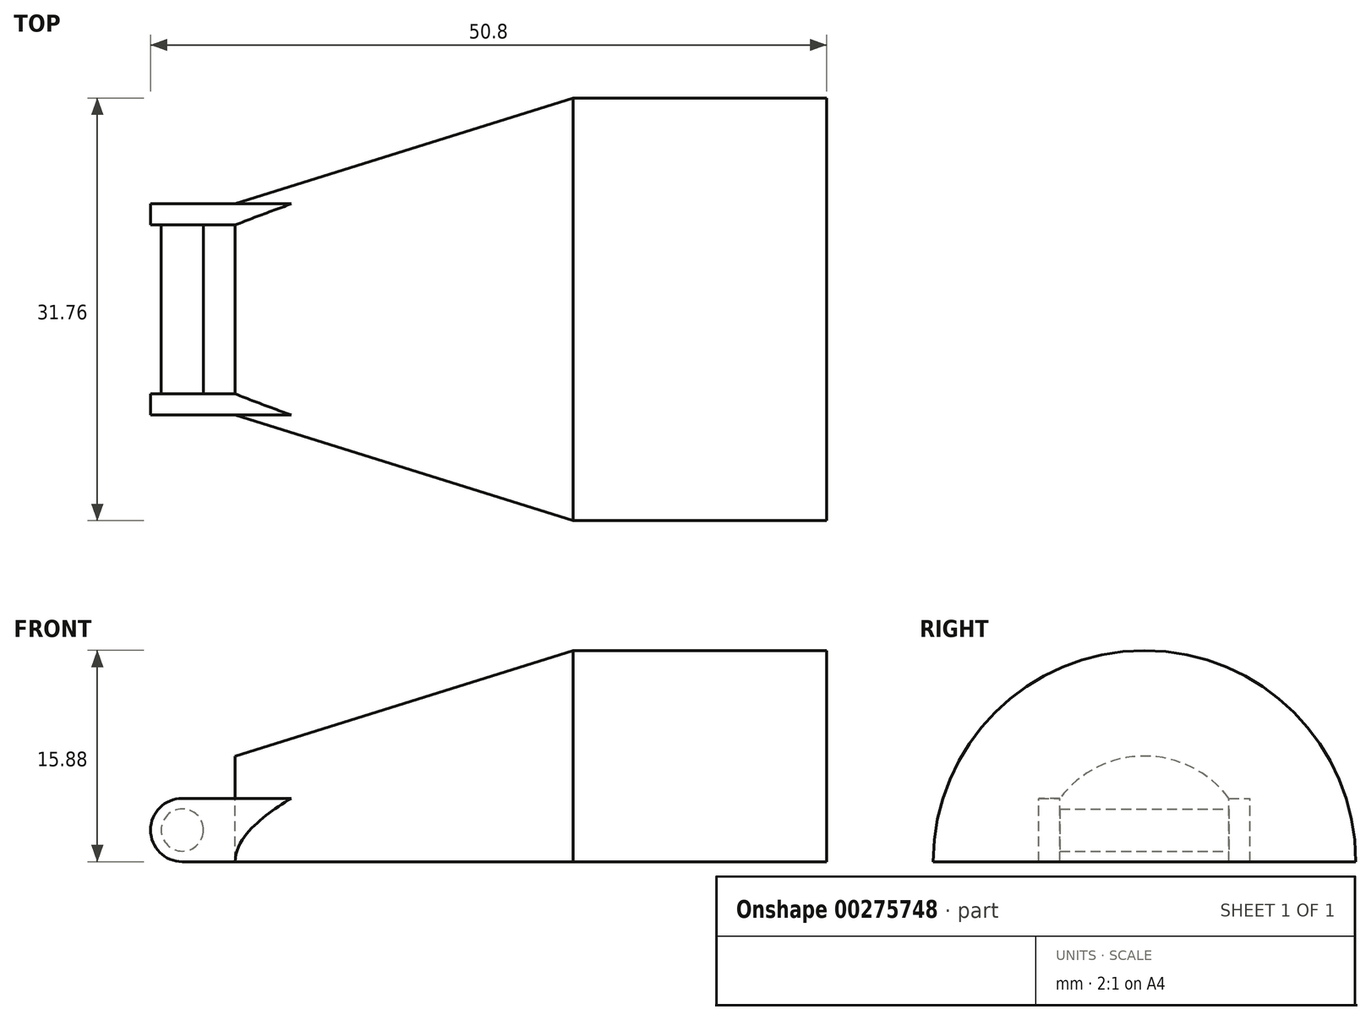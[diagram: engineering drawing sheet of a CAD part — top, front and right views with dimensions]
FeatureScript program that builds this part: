
annotation { "Feature Type Name" : "Feature", "Feature Type Description" : "" }
export const myFeature = defineFeature(function(context is Context, id is Id, definition is map)
    precondition{}
    {
        {
            var Q0;
            Q0=qCreatedBy(makeId("Right.planeOp"),FACE);
            var sketch = newSketch(context, id + "F0", { "sketchPlane" : qUnion([Q0])});
            skLineSegment(sketch, "E0", {"start": v(-15.88, 0) * mm, "end": v(15.88, 0) * mm});
            skCircle(sketch, "E1", {"center": v(0, 0) * mm, "radius": 15.88 * mm});
            skSolve(sketch);
        }
        {
            var Q0;
            Q0=qCreatedBy(makeId("Right.planeOp"),FACE);
            cPlane(context, id + "F1", {"entities" : qUnion([Q0]), "cplaneType" : CPlaneType.OFFSET, "offset" : 25.4 * mm, "oppositeDirection" : true, "width" : 152.4 * mm, "height" : 152.4 * mm});
        }
        {
            var Q0;
            Q0=qCreatedBy(id+"F1.planeOp",FACE);
            var sketch = newSketch(context, id + "F2", { "sketchPlane" : qUnion([Q0])});
            skCircle(sketch, "E2", {"center": v(0, 0) * mm, "radius": 7.94 * mm});
            skLineSegment(sketch, "E3", {"start": v(-7.94, 0) * mm, "end": v(7.94, 0) * mm});
            skSolve(sketch);
        }
        {
            var Q0;
            {var subQ0=sQuery(id+"F2.wireOp",EDGE,"E3");Q0=makeQuery(id+"F2.imprint","IMPRINT",FACE,{"disambiguationData":[TD([[makeQuery(id+"F2.imprint","IMPRINT",EDGE,{"derivedFrom":subQ0}),1.0]])]});}
            var Q1;
            {var subQ0=sQuery(id+"F0.wireOp",EDGE,"E0");Q1=makeQuery(id+"F0.imprint","IMPRINT",FACE,{"disambiguationData":[TD([[makeQuery(id+"F0.imprint","IMPRINT",EDGE,{"derivedFrom":subQ0}),1.0]])]});}
            loft(context, id + "F3", {"sheetProfilesArray" : [{ "sheetProfileEntities" : qUnion([Q0]) }, { "sheetProfileEntities" : qUnion([Q1]) }]});
        }
        {
            var Q0;
            {var subQ0=sQuery(id+"F0.wireOp",EDGE,"E0");Q0=makeQuery(id+"F3.opLoft","CAP_FACE",FACE,{"disambiguationData":[OSD([makeQuery(id+"F0.imprint","IMPRINT",FACE,{"disambiguationData":[TD([[makeQuery(id+"F0.imprint","IMPRINT",EDGE,{"derivedFrom":subQ0}),1.0]])]})])],"isStart":true});}
            extrude(context, id + "F4", {"entities" : qUnion([Q0]), "operationType" : NewBodyOperationType.ADD, "depth" : 19.05 * mm});
        }
        {
            var Q0;
            {var subQ0=sQuery(id+"F2.wireOp",EDGE,"E3");Q0=makeQuery(id+"F3.opLoft","CAP_FACE",FACE,{"disambiguationData":[OSD([makeQuery(id+"F2.imprint","IMPRINT",FACE,{"disambiguationData":[TD([[makeQuery(id+"F2.imprint","IMPRINT",EDGE,{"derivedFrom":subQ0}),1.0]])]})])],"isStart":true});}
            var sketch = newSketch(context, id + "F5", { "sketchPlane" : qUnion([Q0])});
            skLineSegment(sketch, "E4.bottom", {"start": v(-7.94, 0) * mm, "end": v(-6.35, 0) * mm});
            skLineSegment(sketch, "E4.top", {"start": v(-7.94, 4.76) * mm, "end": v(-6.35, 4.76) * mm});
            skLineSegment(sketch, "E4.left", {"start": v(-7.94, 0) * mm, "end": v(-7.94, 4.76) * mm});
            skLineSegment(sketch, "E4.right", {"start": v(-6.35, 0) * mm, "end": v(-6.35, 4.76) * mm});
            skPoint(sketch, "E5.endSnap0", {"position": v(0, 0) * mm});
            skLineSegment(sketch, "E6.MirrorCS", {"start": v(7.94, 0) * mm, "end": v(6.35, 0) * mm});
            skLineSegment(sketch, "E7.MirrorCS", {"start": v(7.94, 0) * mm, "end": v(7.94, 4.76) * mm});
            skLineSegment(sketch, "E8.MirrorCS", {"start": v(6.35, 0) * mm, "end": v(6.35, 4.76) * mm});
            skLineSegment(sketch, "E9.MirrorCS", {"start": v(7.94, 4.76) * mm, "end": v(6.35, 4.76) * mm});
            skSolve(sketch);
        }
        {
            var Q0;
            Q0=qSketchRegion(id+"F5",true);
            extrude(context, id + "F6", {"entities" : qUnion([Q0]), "operationType" : NewBodyOperationType.ADD, "endBound" : BoundingType.SYMMETRIC, "depth" : 12.7 * mm});
        }
        {
            var Q0;
            Q0=makeQuery(id+"F6.opExtrude","SWEPT_FACE",FACE,{"disambiguationData":[OSD([sQuery(id+"F5.wireOp",EDGE,"E4.left")])]});
            var sketch = newSketch(context, id + "F7", { "sketchPlane" : qUnion([Q0])});
            skPoint(sketch, "E10", {"position": v(31.75, 2.38) * mm});
            skLineSegment(sketch, "E11", {"start": v(31.75, 2.38) * mm, "end": v(29.37, 2.38) * mm});
            skCircle(sketch, "E12", {"center": v(29.37, 2.38) * mm, "radius": 2.38 * mm});
            skCircle(sketch, "E13", {"center": v(29.37, 2.38) * mm, "radius": 1.59 * mm});
            skSolve(sketch);
        }
        {
            var Q0;
            {var subQ0=sQuery(id+"F7.wireOp",EDGE,"E12");var subQ1=sQuery(id+"F5.wireOp",EDGE,"E4.left");var subQ2=makeQuery(id+"F6.opExtrude","CAP_EDGE",EDGE,{"disambiguationData":[OSD([subQ1])],"isStart":false});var subQ3=makeQuery(id+"F7.imprint","INTERSECT",VERTEX,{"derivedFrom":[subQ2,subQ0]});Q0=makeQuery(id+"F7.imprint","IMPRINT",FACE,{"disambiguationData":[TD([[makeQuery(id+"F7.imprint","IMPRINT",EDGE,{"disambiguationData":[TD([[subQ3,-1.0]])],"derivedFrom":subQ0}),-1.0]])]});}
            var Q1;
            {var subQ0=sQuery(id+"F7.wireOp",EDGE,"E12");var subQ1=sQuery(id+"F5.wireOp",EDGE,"E4.left");var subQ2=makeQuery(id+"F6.opExtrude","CAP_EDGE",EDGE,{"disambiguationData":[OSD([subQ1])],"isStart":false});var subQ3=makeQuery(id+"F7.imprint","INTERSECT",VERTEX,{"derivedFrom":[subQ2,subQ0]});Q1=makeQuery(id+"F7.imprint","IMPRINT",FACE,{"disambiguationData":[TD([[makeQuery(id+"F7.imprint","IMPRINT",EDGE,{"disambiguationData":[TD([[subQ3,1.0]])],"derivedFrom":subQ0}),-1.0]])]});}
            extrude(context, id + "F8", {"entities" : qUnion([Q0, Q1]), "operationType" : NewBodyOperationType.REMOVE, "oppositeDirection" : true, "depth" : 25.4 * mm});
        }
        {
            var Q0;
            Q0=makeQuery(id+"F7.imprint","IMPRINT",FACE,{"disambiguationData":[TD([[makeQuery(id+"F7.imprint","IMPRINT",EDGE,{"derivedFrom":sQuery(id+"F7.wireOp",EDGE,"E13")}),1.0]])]});
            extrude(context, id + "F9", {"entities" : qUnion([Q0]), "operationType" : NewBodyOperationType.ADD, "oppositeDirection" : true, "depth" : 15.88 * mm});
        }
    });
